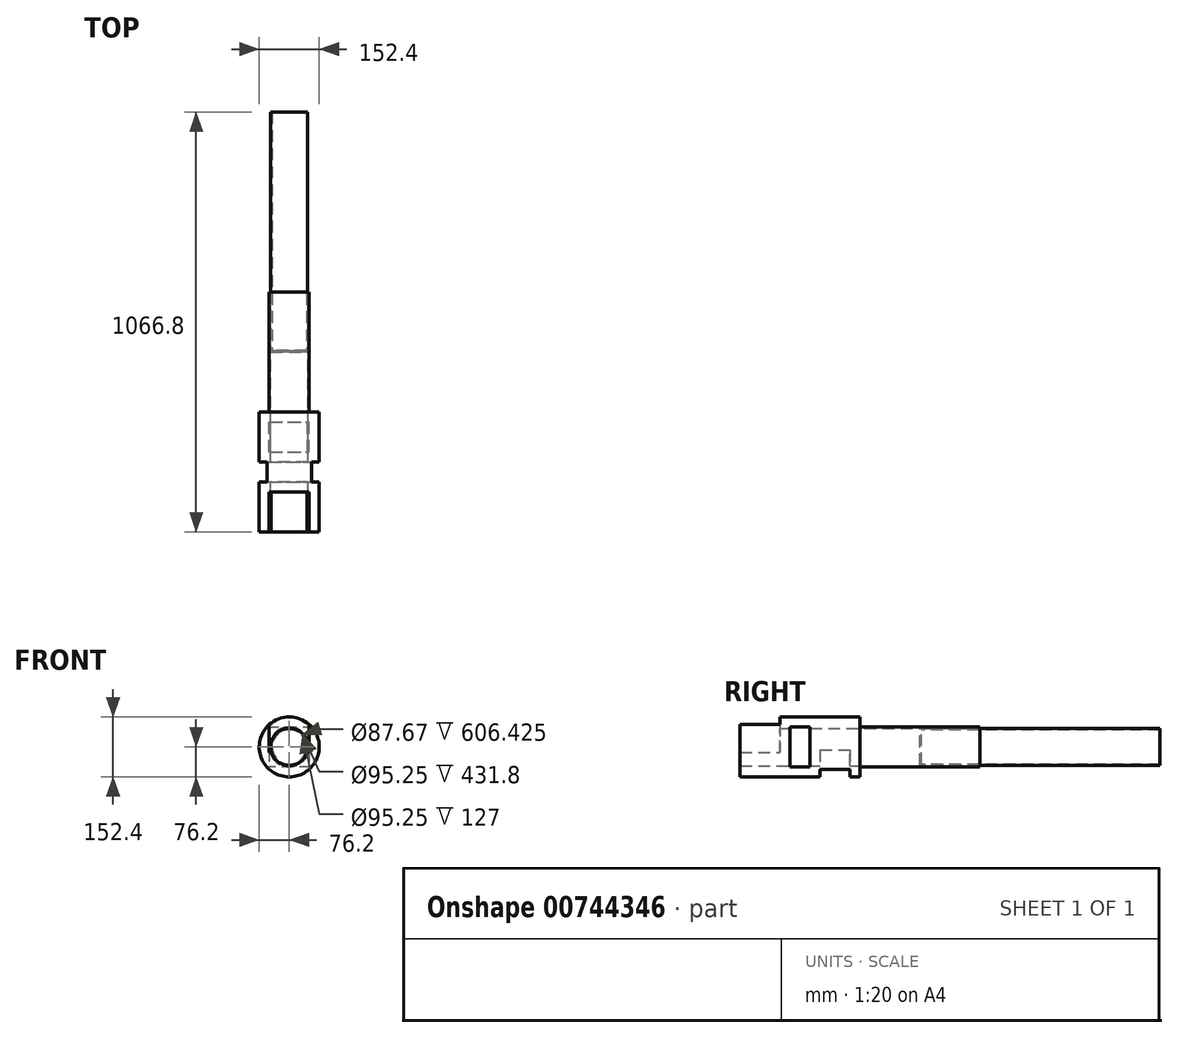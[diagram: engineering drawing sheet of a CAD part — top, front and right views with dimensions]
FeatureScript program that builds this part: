
annotation { "Feature Type Name" : "Feature", "Feature Type Description" : "" }
export const myFeature = defineFeature(function(context is Context, id is Id, definition is map)
    precondition{}
    {
        {
            var Q0;
            Q0=qCreatedBy(makeId("Front.planeOp"),FACE);
            var sketch = newSketch(context, id + "F0", { "sketchPlane" : qUnion([Q0])});
            skCircle(sketch, "E0", {"center": v(0, 0) * mm, "radius": 50.8 * mm});
            skCircle(sketch, "E1.0", {"center": v(0, 0) * mm, "radius": 47.63 * mm});
            skSolve(sketch);
        }
        {
            var Q0;
            Q0 = qSketchRegion(id + "F0", true);
            extrude(context, id + "F1", {"entities" : qUnion([Q0]), "endBound" : BoundingType.SYMMETRIC, "depth" : 609.6 * mm, "offsetDistance" : 25.4 * mm});
        }
        {
            var Q0;
            Q0=qCreatedBy(makeId("Front.planeOp"),FACE);
            var sketch = newSketch(context, id + "F2", { "sketchPlane" : qUnion([Q0])});
            skCircle(sketch, "E2", {"center": v(0, 0) * mm, "radius": 47 * mm});
            skCircle(sketch, "E3.0", {"center": v(0, 0) * mm, "radius": 43.83 * mm});
            skSolve(sketch);
        }
        {
            var Q0;
            Q0 = qSketchRegion(id + "F2", true);
            extrude(context, id + "F3", {"entities" : qUnion([Q0]), "oppositeDirection" : true, "depth" : 762 * mm, "offsetDistance" : 25.4 * mm, "hasSecondDirection" : true, "secondDirectionOppositeDirection" : true, "secondDirectionDepth" : 152.4 * mm});
        }
        {
            var Q0;
            Q0=makeQuery(id+"F2.imprint","IMPRINT",FACE,{"disambiguationData":[TD([[makeQuery(id+"F2.imprint","IMPRINT",EDGE,{"derivedFrom":sQuery(id+"F2.wireOp",EDGE,"E3.0")}),1.0]])]});
            extrude(context, id + "F4", {"entities" : qUnion([Q0]), "operationType" : NewBodyOperationType.ADD, "oppositeDirection" : true, "depth" : 155.57 * mm, "offsetDistance" : 25.4 * mm, "hasSecondDirection" : true, "secondDirectionOppositeDirection" : true, "secondDirectionDepth" : 152.4 * mm});
        }
        {
            var Q0;
            Q0=qCreatedBy(makeId("Front.planeOp"),FACE);
            var sketch = newSketch(context, id + "F5", { "sketchPlane" : qUnion([Q0])});
            skCircle(sketch, "E4", {"center": v(0, 0) * mm, "radius": 76.2 * mm});
            skCircle(sketch, "E5", {"center": v(0, 0) * mm, "radius": 50.8 * mm});
            skSolve(sketch);
        }
        {
            var Q0;
            Q0=makeQuery(id+"F5.imprint","IMPRINT",FACE,{"disambiguationData":[TD([[makeQuery(id+"F5.imprint","IMPRINT",EDGE,{"derivedFrom":sQuery(id+"F5.wireOp",EDGE,"E4")}),1.0]])]});
            extrude(context, id + "F6", {"entities" : qUnion([Q0]), "operationType" : NewBodyOperationType.ADD, "depth" : 304.8 * mm, "offsetDistance" : 25.4 * mm});
        }
        {
            var Q0;
            Q0=qCreatedBy(makeId("Front.planeOp"),FACE);
            var sketch = newSketch(context, id + "F7", { "sketchPlane" : qUnion([Q0])});
            skLineSegment(sketch, "E6.bottom", {"start": v(-76.2, 50.8) * mm, "end": v(76.2, 50.8) * mm});
            skLineSegment(sketch, "E6.top", {"start": v(-76.2, -50.8) * mm, "end": v(76.2, -50.8) * mm});
            skLineSegment(sketch, "E6.left", {"start": v(-76.2, 50.8) * mm, "end": v(-76.2, -50.8) * mm});
            skLineSegment(sketch, "E6.right", {"start": v(76.2, 50.8) * mm, "end": v(76.2, -50.8) * mm});
            skPoint(sketch, "E6.middle", {"position": v(0, 0) * mm});
            skSolve(sketch);
        }
        {
            var Q0;
            Q0=makeQuery(id+"F7.imprint","IMPRINT",FACE,{"disambiguationData":[TD([[makeQuery(id+"F7.imprint","IMPRINT",EDGE,{"derivedFrom":sQuery(id+"F7.wireOp",EDGE,"E6.bottom")}),-1.0]])]});
            extrude(context, id + "F8", {"entities" : qUnion([Q0]), "operationType" : NewBodyOperationType.REMOVE, "depth" : 177.8 * mm, "offsetDistance" : 25.4 * mm, "hasDraft" : true, "draftAngle" : 0 * degree, "hasSecondDirection" : true, "secondDirectionOppositeDirection" : false, "secondDirectionDepth" : 127 * mm});
        }
        {
            var Q0;
            Q0=qCreatedBy(makeId("Front.planeOp"),FACE);
            var sketch = newSketch(context, id + "F9", { "sketchPlane" : qUnion([Q0])});
            skLineSegment(sketch, "E7.bottom", {"start": v(50.8, 138.87) * mm, "end": v(-50.8, 138.87) * mm});
            skLineSegment(sketch, "E7.top", {"start": v(50.8, -13.53) * mm, "end": v(-50.8, -13.53) * mm});
            skLineSegment(sketch, "E7.left", {"start": v(50.8, 138.87) * mm, "end": v(50.8, -13.53) * mm});
            skLineSegment(sketch, "E7.right", {"start": v(-50.8, 138.87) * mm, "end": v(-50.8, -13.53) * mm});
            skPoint(sketch, "E7.middle", {"position": v(0, 62.67) * mm});
            skSolve(sketch);
        }
        {
            var Q0;
            Q0=makeQuery(id+"F9.imprint","IMPRINT",FACE,{"disambiguationData":[TD([[makeQuery(id+"F9.imprint","IMPRINT",EDGE,{"derivedFrom":sQuery(id+"F9.wireOp",EDGE,"E7.bottom")}),1.0]])]});
            extrude(context, id + "F10", {"entities" : qUnion([Q0]), "operationType" : NewBodyOperationType.REMOVE, "depth" : 304.8 * mm, "offsetDistance" : 25.4 * mm, "hasSecondDirection" : true, "secondDirectionOppositeDirection" : false, "secondDirectionDepth" : 203.2 * mm});
        }
        {
            var Q0;
            Q0=qCreatedBy(makeId("Front.planeOp"),FACE);
            var sketch = newSketch(context, id + "F11", { "sketchPlane" : qUnion([Q0])});
            skLineSegment(sketch, "E8.bottom", {"start": v(-50.8, -8) * mm, "end": v(50.8, -8) * mm});
            skLineSegment(sketch, "E8.top", {"start": v(-50.8, -185.8) * mm, "end": v(50.8, -185.8) * mm});
            skLineSegment(sketch, "E8.left", {"start": v(-50.8, -8) * mm, "end": v(-50.8, -185.8) * mm});
            skLineSegment(sketch, "E8.right", {"start": v(50.8, -8) * mm, "end": v(50.8, -185.8) * mm});
            skPoint(sketch, "E8.middle", {"position": v(0, -96.9) * mm});
            skSolve(sketch);
        }
        {
            var Q0;
            Q0=makeQuery(id+"F11.imprint","IMPRINT",FACE,{"disambiguationData":[TD([[makeQuery(id+"F11.imprint","IMPRINT",EDGE,{"derivedFrom":sQuery(id+"F11.wireOp",EDGE,"E8.bottom")}),-1.0]])]});
            extrude(context, id + "F12", {"entities" : qUnion([Q0]), "operationType" : NewBodyOperationType.REMOVE, "depth" : 101.6 * mm, "offsetDistance" : 25.4 * mm, "hasSecondDirection" : true, "secondDirectionOppositeDirection" : false, "secondDirectionDepth" : 25.4 * mm});
        }
    });
